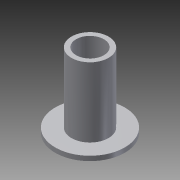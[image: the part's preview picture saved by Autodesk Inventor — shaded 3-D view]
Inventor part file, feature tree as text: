
AUTODESK INVENTOR PART (.ipt)
format: ipt  version: 2014 (Build 180170000, 170)  size: 88,064 bytes
history: native  units: mm
features: extrude x2, sketch x2
ambient origin geometry x8: Origin, YZ Plane, XZ Plane, XY Plane, X Axis, Y Axis, Z Axis, Center Point
bodies: Solid1 (feature_tree)
feature tree (4):
  extrude  "Extrusion1"  Depth=15.0mm
  extrude  "Extrusion2"  Depth=15.0mm
  sketch  "Sketch1"  dims[d0=6.0mm d1=15.0mm]
  sketch  "Sketch2"  dims[d2=1.0mm d3=0.0mm d4=8.0mm d5=15.0mm d6=0.0mm]
